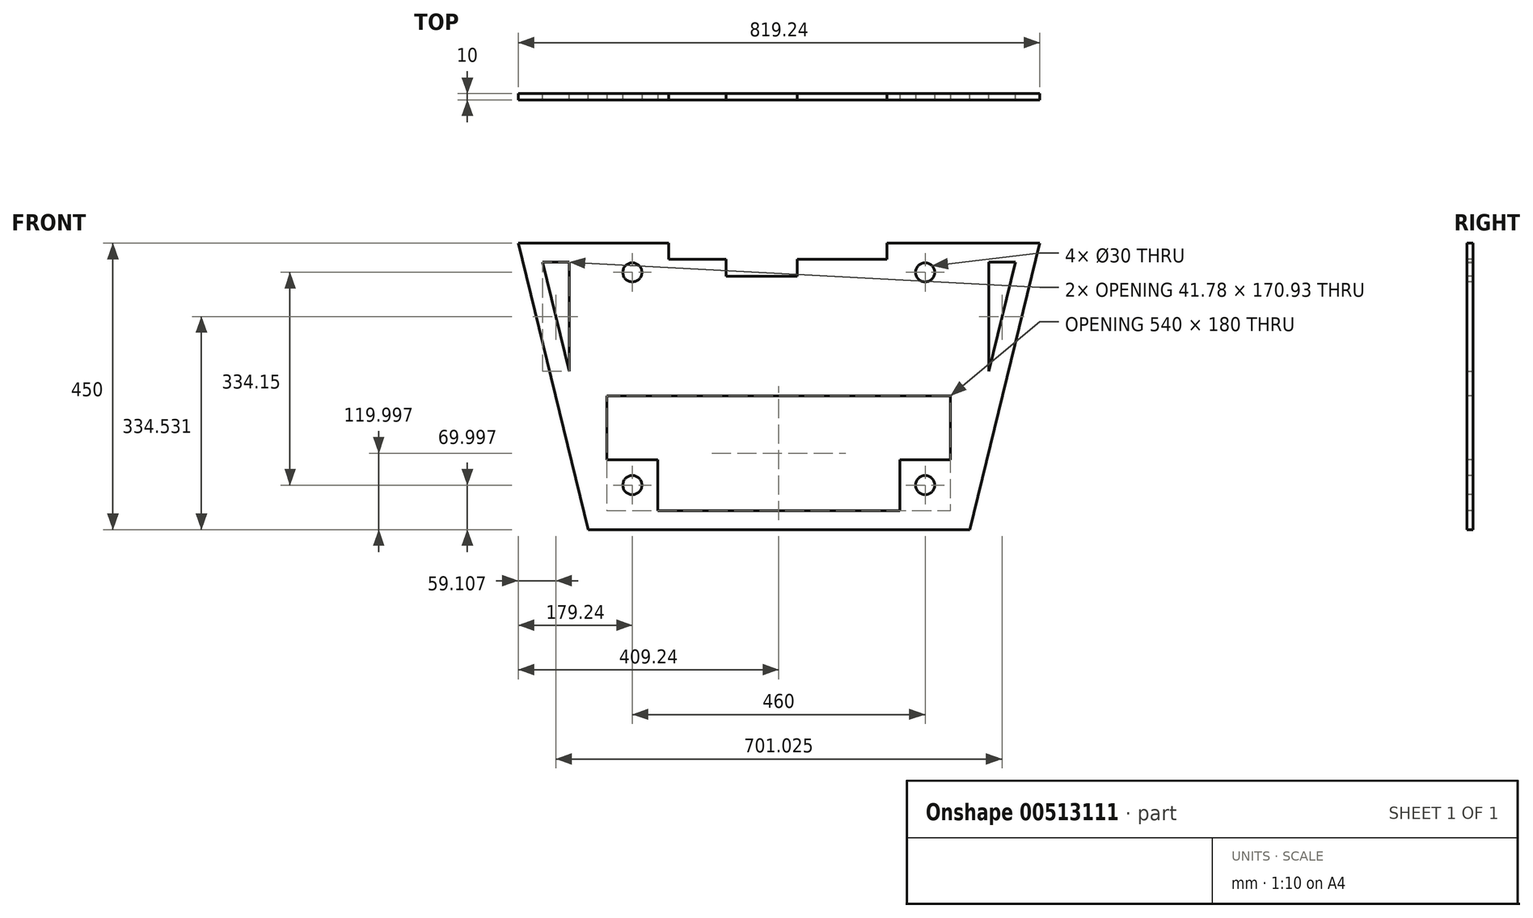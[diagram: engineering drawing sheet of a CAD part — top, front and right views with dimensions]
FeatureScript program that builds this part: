
annotation { "Feature Type Name" : "Feature", "Feature Type Description" : "" }
export const myFeature = defineFeature(function(context is Context, id is Id, definition is map)
    precondition{}
    {
        {
            var Q0;
            Q0=qCreatedBy(makeId("Front.planeOp"),FACE);
            var sketch = newSketch(context, id + "F0", { "sketchPlane" : qUnion([Q0])});
            skLineSegment(sketch, "E0.1", {"start": v(-436.34, 213.95) * mm, "end": v(-436.34, -176.05) * mm});
            skLineSegment(sketch, "E0.3", {"start": v(103.66, 213.95) * mm, "end": v(103.66, -176.05) * mm});
            skLineSegment(sketch, "E1", {"start": v(-465.58, -206.05) * mm, "end": v(133.66, -206.05) * mm});
            skLineSegment(sketch, "E2", {"start": v(-436.34, -176.05) * mm, "end": v(103.66, -176.05) * mm});
            skLineSegment(sketch, "E3", {"start": v(-436.34, 213.95) * mm, "end": v(103.66, 213.95) * mm});
            skLineSegment(sketch, "E4", {"start": v(-465.58, 243.95) * mm, "end": v(133.66, 243.95) * mm});
            skLineSegment(sketch, "E5", {"start": v(-465.58, 243.95) * mm, "end": v(-575.58, 243.95) * mm});
            skLineSegment(sketch, "E6", {"start": v(133.66, 243.95) * mm, "end": v(243.66, 243.95) * mm});
            skLineSegment(sketch, "E7", {"start": v(-575.58, 243.95) * mm, "end": v(-465.58, -206.05) * mm});
            skLineSegment(sketch, "E8", {"start": v(243.66, 243.95) * mm, "end": v(133.66, -206.05) * mm});
            skLineSegment(sketch, "E9.0", {"start": v(-537.36, 213.95) * mm, "end": v(-495.58, 43.02) * mm});
            skLineSegment(sketch, "E9.1", {"start": v(-495.58, 213.95) * mm, "end": v(-537.36, 213.95) * mm});
            skLineSegment(sketch, "E9.2", {"start": v(-495.58, 213.95) * mm, "end": v(-495.58, 43.02) * mm});
            skLineSegment(sketch, "E10.0", {"start": v(205.44, 213.95) * mm, "end": v(163.66, 43.02) * mm});
            skLineSegment(sketch, "E10.1", {"start": v(163.66, 213.95) * mm, "end": v(205.44, 213.95) * mm});
            skLineSegment(sketch, "E10.2", {"start": v(163.66, 213.95) * mm, "end": v(163.66, 43.02) * mm});
            skSolve(sketch);
        }
        {
            var Q0;
            Q0=makeQuery(id+"F0.imprint","IMPRINT",FACE,{"disambiguationData":[TD([[makeQuery(id+"F0.imprint","IMPRINT",EDGE,{"derivedFrom":sQuery(id+"F0.wireOp",EDGE,"E0.1")}),-1.0]])]});
            extrude(context, id + "F1", {"entities" : qUnion([Q0]), "depth" : 10 * mm, "offsetDistance" : 25 * mm});
        }
        {
            var Q0;
            Q0=makeQuery(id+"F1.opExtrude","CAP_FACE",FACE,{"disambiguationData":[OSD([sQuery(id+"F0.wireOp",EDGE,"E0.1"),sQuery(id+"F0.wireOp",EDGE,"E0.3"),sQuery(id+"F0.wireOp",EDGE,"E1"),sQuery(id+"F0.wireOp",EDGE,"E2"),sQuery(id+"F0.wireOp",EDGE,"E3"),sQuery(id+"F0.wireOp",EDGE,"E4"),sQuery(id+"F0.wireOp",EDGE,"E5"),sQuery(id+"F0.wireOp",EDGE,"E6"),sQuery(id+"F0.wireOp",EDGE,"E7"),sQuery(id+"F0.wireOp",EDGE,"E8"),sQuery(id+"F0.wireOp",EDGE,"E9.0"),sQuery(id+"F0.wireOp",EDGE,"E9.1"),sQuery(id+"F0.wireOp",EDGE,"E9.2"),sQuery(id+"F0.wireOp",EDGE,"E10.0"),sQuery(id+"F0.wireOp",EDGE,"E10.1"),sQuery(id+"F0.wireOp",EDGE,"E10.2")])],"isStart":false});
            var sketch = newSketch(context, id + "F2", { "sketchPlane" : qUnion([Q0])});
            skLineSegment(sketch, "E11.bottom", {"start": v(-436.34, 213.95) * mm, "end": v(-356.34, 213.95) * mm});
            skLineSegment(sketch, "E11.top", {"start": v(-436.34, 133.95) * mm, "end": v(-356.34, 133.95) * mm});
            skLineSegment(sketch, "E11.left", {"start": v(-436.34, 213.95) * mm, "end": v(-436.34, 133.95) * mm});
            skLineSegment(sketch, "E11.right", {"start": v(-356.34, 213.95) * mm, "end": v(-356.34, 133.95) * mm});
            skLineSegment(sketch, "E12.bottom", {"start": v(103.66, 213.95) * mm, "end": v(23.66, 213.95) * mm});
            skLineSegment(sketch, "E12.top", {"start": v(103.66, 133.95) * mm, "end": v(23.66, 133.95) * mm});
            skLineSegment(sketch, "E12.left", {"start": v(103.66, 213.95) * mm, "end": v(103.66, 133.95) * mm});
            skLineSegment(sketch, "E12.right", {"start": v(23.66, 213.95) * mm, "end": v(23.66, 133.95) * mm});
            skLineSegment(sketch, "E13.bottom", {"start": v(-436.34, -176.05) * mm, "end": v(-356.34, -176.05) * mm});
            skLineSegment(sketch, "E13.top", {"start": v(-436.34, -96.05) * mm, "end": v(-356.34, -96.05) * mm});
            skLineSegment(sketch, "E13.left", {"start": v(-436.34, -176.05) * mm, "end": v(-436.34, -96.05) * mm});
            skLineSegment(sketch, "E13.right", {"start": v(-356.34, -176.05) * mm, "end": v(-356.34, -96.05) * mm});
            skLineSegment(sketch, "E14.bottom", {"start": v(103.66, -176.05) * mm, "end": v(23.66, -176.05) * mm});
            skLineSegment(sketch, "E14.top", {"start": v(103.66, -96.05) * mm, "end": v(23.66, -96.05) * mm});
            skLineSegment(sketch, "E14.left", {"start": v(103.66, -176.05) * mm, "end": v(103.66, -96.05) * mm});
            skLineSegment(sketch, "E14.right", {"start": v(23.66, -176.05) * mm, "end": v(23.66, -96.05) * mm});
            skCircle(sketch, "E15", {"center": v(-396.34, -136.05) * mm, "radius": 15 * mm});
            skCircle(sketch, "E16", {"center": v(-396.34, 198.1) * mm, "radius": 15 * mm});
            skCircle(sketch, "E17", {"center": v(63.66, 198.1) * mm, "radius": 15 * mm});
            skCircle(sketch, "E18", {"center": v(63.66, -136.05) * mm, "radius": 15 * mm});
            skLineSegment(sketch, "E19", {"start": v(-356.34, 213.95) * mm, "end": v(-396.34, 243.95) * mm});
            skLineSegment(sketch, "E20", {"start": v(-356.34, 133.95) * mm, "end": v(23.66, 133.95) * mm});
            skLineSegment(sketch, "E21", {"start": v(23.66, 213.95) * mm, "end": v(63.66, 243.95) * mm});
            skLineSegment(sketch, "E22", {"start": v(-356.34, 213.95) * mm, "end": v(-249.67, 133.95) * mm});
            skLineSegment(sketch, "E23", {"start": v(23.66, 213.95) * mm, "end": v(-83, 133.95) * mm});
            skLineSegment(sketch, "E24", {"start": v(-396.34, 243.95) * mm, "end": v(63.66, 243.95) * mm});
            skSolve(sketch);
        }
        {
            var Q0;
            Q0=makeQuery(id+"F2.imprint","IMPRINT",FACE,{"disambiguationData":[TD([[makeQuery(id+"F2.imprint","IMPRINT",EDGE,{"derivedFrom":sQuery(id+"F2.wireOp",EDGE,"E11.bottom")}),-1.0]])]});
            var Q1;
            Q1=makeQuery(id+"F2.imprint","IMPRINT",FACE,{"disambiguationData":[TD([[makeQuery(id+"F2.imprint","IMPRINT",EDGE,{"derivedFrom":sQuery(id+"F2.wireOp",EDGE,"E12.bottom")}),-1.0]])]});
            var Q2;
            Q2=makeQuery(id+"F2.imprint","IMPRINT",FACE,{"disambiguationData":[TD([[makeQuery(id+"F2.imprint","IMPRINT",EDGE,{"derivedFrom":sQuery(id+"F2.wireOp",EDGE,"E14.bottom")}),1.0]])]});
            var Q3;
            Q3=makeQuery(id+"F2.imprint","IMPRINT",FACE,{"disambiguationData":[TD([[makeQuery(id+"F2.imprint","IMPRINT",EDGE,{"derivedFrom":sQuery(id+"F2.wireOp",EDGE,"E13.bottom")}),1.0]])]});
            extrude(context, id + "F3", {"entities" : qUnion([Q0, Q1, Q2, Q3]), "operationType" : NewBodyOperationType.ADD, "oppositeDirection" : true, "depth" : 10 * mm, "offsetDistance" : 25 * mm});
        }
        {
            var Q0;
            Q0=makeQuery(id+"F3.boolean.opBoolean","MERGE",FACE,{"derivedFrom":[makeQuery(id+"F1.opExtrude","CAP_FACE",FACE,{"disambiguationData":[OSD([sQuery(id+"F0.wireOp",EDGE,"E0.1"),sQuery(id+"F0.wireOp",EDGE,"E0.3"),sQuery(id+"F0.wireOp",EDGE,"E1"),sQuery(id+"F0.wireOp",EDGE,"E2"),sQuery(id+"F0.wireOp",EDGE,"E3"),sQuery(id+"F0.wireOp",EDGE,"E4"),sQuery(id+"F0.wireOp",EDGE,"E5"),sQuery(id+"F0.wireOp",EDGE,"E6"),sQuery(id+"F0.wireOp",EDGE,"E7"),sQuery(id+"F0.wireOp",EDGE,"E8"),sQuery(id+"F0.wireOp",EDGE,"E9.0"),sQuery(id+"F0.wireOp",EDGE,"E9.1"),sQuery(id+"F0.wireOp",EDGE,"E9.2"),sQuery(id+"F0.wireOp",EDGE,"E10.0"),sQuery(id+"F0.wireOp",EDGE,"E10.1"),sQuery(id+"F0.wireOp",EDGE,"E10.2")])],"isStart":false}),makeQuery(id+"F3.opExtrude","CAP_FACE",FACE,{"disambiguationData":[OSD([sQuery(id+"F2.wireOp",EDGE,"E11.bottom"),sQuery(id+"F2.wireOp",EDGE,"E11.top"),sQuery(id+"F2.wireOp",EDGE,"E11.left"),sQuery(id+"F2.wireOp",EDGE,"E11.right"),sQuery(id+"F2.wireOp",EDGE,"E16")])],"isStart":true}),makeQuery(id+"F3.opExtrude","CAP_FACE",FACE,{"disambiguationData":[OSD([sQuery(id+"F2.wireOp",EDGE,"E12.bottom"),sQuery(id+"F2.wireOp",EDGE,"E12.top"),sQuery(id+"F2.wireOp",EDGE,"E12.left"),sQuery(id+"F2.wireOp",EDGE,"E12.right"),sQuery(id+"F2.wireOp",EDGE,"E17")])],"isStart":true}),makeQuery(id+"F3.opExtrude","CAP_FACE",FACE,{"disambiguationData":[OSD([sQuery(id+"F2.wireOp",EDGE,"E13.bottom"),sQuery(id+"F2.wireOp",EDGE,"E13.top"),sQuery(id+"F2.wireOp",EDGE,"E13.left"),sQuery(id+"F2.wireOp",EDGE,"E13.right"),sQuery(id+"F2.wireOp",EDGE,"E15")])],"isStart":true}),makeQuery(id+"F3.opExtrude","CAP_FACE",FACE,{"disambiguationData":[OSD([sQuery(id+"F2.wireOp",EDGE,"E14.bottom"),sQuery(id+"F2.wireOp",EDGE,"E14.top"),sQuery(id+"F2.wireOp",EDGE,"E14.left"),sQuery(id+"F2.wireOp",EDGE,"E14.right"),sQuery(id+"F2.wireOp",EDGE,"E18")])],"isStart":true})]});
            var sketch = newSketch(context, id + "F4", { "sketchPlane" : qUnion([Q0])});
            skLineSegment(sketch, "E25", {"start": v(-356.34, 133.95) * mm, "end": v(23.66, 133.95) * mm});
            skLineSegment(sketch, "E26", {"start": v(-167.95, 292.5) * mm, "end": v(-335.9, 292.5) * mm});
            skLineSegment(sketch, "E27", {"start": v(-167.95, 292.5) * mm, "end": v(0, 292.5) * mm});
            skPoint(sketch, "E28.start.orphan", {"position": v(-166.34, 213.95) * mm});
            skLineSegment(sketch, "E29", {"start": v(-356.34, 243.95) * mm, "end": v(23.66, 243.95) * mm});
            skLineSegment(sketch, "E30", {"start": v(-286.97, 218.5) * mm, "end": v(3.6, 218.5) * mm});
            skLineSegment(sketch, "E31", {"start": v(-286.97, 218.5) * mm, "end": v(-339, 218.5) * mm});
            skPoint(sketch, "E32.orphan", {"position": v(-335.9, 213.95) * mm});
            skPoint(sketch, "E33.orphan", {"position": v(0, 213.95) * mm});
            skLineSegment(sketch, "E34", {"start": v(-339, 218.5) * mm, "end": v(-339, 243.95) * mm});
            skLineSegment(sketch, "E35", {"start": v(3.6, 218.5) * mm, "end": v(3.6, 243.95) * mm});
            skSolve(sketch);
        }
        {
            var Q0;
            Q0=makeQuery(id+"F3.boolean.opBoolean","MERGE",FACE,{"derivedFrom":[makeQuery(id+"F1.opExtrude","CAP_FACE",FACE,{"disambiguationData":[OSD([sQuery(id+"F0.wireOp",EDGE,"E0.1"),sQuery(id+"F0.wireOp",EDGE,"E0.3"),sQuery(id+"F0.wireOp",EDGE,"E1"),sQuery(id+"F0.wireOp",EDGE,"E2"),sQuery(id+"F0.wireOp",EDGE,"E3"),sQuery(id+"F0.wireOp",EDGE,"E4"),sQuery(id+"F0.wireOp",EDGE,"E5"),sQuery(id+"F0.wireOp",EDGE,"E6"),sQuery(id+"F0.wireOp",EDGE,"E7"),sQuery(id+"F0.wireOp",EDGE,"E8"),sQuery(id+"F0.wireOp",EDGE,"E9.0"),sQuery(id+"F0.wireOp",EDGE,"E9.1"),sQuery(id+"F0.wireOp",EDGE,"E9.2"),sQuery(id+"F0.wireOp",EDGE,"E10.0"),sQuery(id+"F0.wireOp",EDGE,"E10.1"),sQuery(id+"F0.wireOp",EDGE,"E10.2")])],"isStart":false}),makeQuery(id+"F3.opExtrude","CAP_FACE",FACE,{"disambiguationData":[OSD([sQuery(id+"F2.wireOp",EDGE,"E11.bottom"),sQuery(id+"F2.wireOp",EDGE,"E11.top"),sQuery(id+"F2.wireOp",EDGE,"E11.left"),sQuery(id+"F2.wireOp",EDGE,"E11.right"),sQuery(id+"F2.wireOp",EDGE,"E16")])],"isStart":true}),makeQuery(id+"F3.opExtrude","CAP_FACE",FACE,{"disambiguationData":[OSD([sQuery(id+"F2.wireOp",EDGE,"E12.bottom"),sQuery(id+"F2.wireOp",EDGE,"E12.top"),sQuery(id+"F2.wireOp",EDGE,"E12.left"),sQuery(id+"F2.wireOp",EDGE,"E12.right"),sQuery(id+"F2.wireOp",EDGE,"E17")])],"isStart":true}),makeQuery(id+"F3.opExtrude","CAP_FACE",FACE,{"disambiguationData":[OSD([sQuery(id+"F2.wireOp",EDGE,"E13.bottom"),sQuery(id+"F2.wireOp",EDGE,"E13.top"),sQuery(id+"F2.wireOp",EDGE,"E13.left"),sQuery(id+"F2.wireOp",EDGE,"E13.right"),sQuery(id+"F2.wireOp",EDGE,"E15")])],"isStart":true}),makeQuery(id+"F3.opExtrude","CAP_FACE",FACE,{"disambiguationData":[OSD([sQuery(id+"F2.wireOp",EDGE,"E14.bottom"),sQuery(id+"F2.wireOp",EDGE,"E14.top"),sQuery(id+"F2.wireOp",EDGE,"E14.left"),sQuery(id+"F2.wireOp",EDGE,"E14.right"),sQuery(id+"F2.wireOp",EDGE,"E18")])],"isStart":true})]});
            var sketch = newSketch(context, id + "F5", { "sketchPlane" : qUnion([Q0])});
            skLineSegment(sketch, "E36.bottom", {"start": v(-356.34, 213.95) * mm, "end": v(23.66, 213.95) * mm});
            skLineSegment(sketch, "E36.top", {"start": v(-356.34, 133.95) * mm, "end": v(23.66, 133.95) * mm});
            skLineSegment(sketch, "E36.left", {"start": v(-356.34, 213.95) * mm, "end": v(-356.34, 133.95) * mm});
            skLineSegment(sketch, "E36.right", {"start": v(23.66, 213.95) * mm, "end": v(23.66, 133.95) * mm});
            skSolve(sketch);
        }
        {
            var Q0;
            Q0=makeQuery(id+"F5.imprint","IMPRINT",FACE,{"disambiguationData":[TD([[makeQuery(id+"F5.imprint","IMPRINT",EDGE,{"derivedFrom":sQuery(id+"F5.wireOp",EDGE,"E36.bottom")}),-1.0]])]});
            extrude(context, id + "F6", {"entities" : qUnion([Q0]), "operationType" : NewBodyOperationType.ADD, "oppositeDirection" : true, "depth" : 10 * mm, "offsetDistance" : 25 * mm});
        }
        {
            var Q0;
            Q0=makeQuery(id+"F4.imprint","IMPRINT",FACE,{"disambiguationData":[TD([[makeQuery(id+"F4.imprint","IMPRINT",EDGE,{"derivedFrom":sQuery(id+"F4.wireOp",EDGE,"E30")}),1.0]])]});
            extrude(context, id + "F7", {"entities" : qUnion([Q0]), "operationType" : NewBodyOperationType.REMOVE, "oppositeDirection" : true, "depth" : 25 * mm, "offsetDistance" : 25 * mm});
        }
        {
            var Q0;
            Q0=makeQuery(id+"F6.boolean.opBoolean","MERGE",FACE,{"derivedFrom":[makeQuery(id+"F3.boolean.opBoolean","MERGE",FACE,{"derivedFrom":[makeQuery(id+"F1.opExtrude","CAP_FACE",FACE,{"disambiguationData":[OSD([sQuery(id+"F0.wireOp",EDGE,"E0.1"),sQuery(id+"F0.wireOp",EDGE,"E0.3"),sQuery(id+"F0.wireOp",EDGE,"E1"),sQuery(id+"F0.wireOp",EDGE,"E2"),sQuery(id+"F0.wireOp",EDGE,"E3"),sQuery(id+"F0.wireOp",EDGE,"E4"),sQuery(id+"F0.wireOp",EDGE,"E5"),sQuery(id+"F0.wireOp",EDGE,"E6"),sQuery(id+"F0.wireOp",EDGE,"E7"),sQuery(id+"F0.wireOp",EDGE,"E8"),sQuery(id+"F0.wireOp",EDGE,"E9.0"),sQuery(id+"F0.wireOp",EDGE,"E9.1"),sQuery(id+"F0.wireOp",EDGE,"E9.2"),sQuery(id+"F0.wireOp",EDGE,"E10.0"),sQuery(id+"F0.wireOp",EDGE,"E10.1"),sQuery(id+"F0.wireOp",EDGE,"E10.2")])],"isStart":false}),makeQuery(id+"F3.opExtrude","CAP_FACE",FACE,{"disambiguationData":[OSD([sQuery(id+"F2.wireOp",EDGE,"E11.bottom"),sQuery(id+"F2.wireOp",EDGE,"E11.top"),sQuery(id+"F2.wireOp",EDGE,"E11.left"),sQuery(id+"F2.wireOp",EDGE,"E11.right"),sQuery(id+"F2.wireOp",EDGE,"E16")])],"isStart":true}),makeQuery(id+"F3.opExtrude","CAP_FACE",FACE,{"disambiguationData":[OSD([sQuery(id+"F2.wireOp",EDGE,"E12.bottom"),sQuery(id+"F2.wireOp",EDGE,"E12.top"),sQuery(id+"F2.wireOp",EDGE,"E12.left"),sQuery(id+"F2.wireOp",EDGE,"E12.right"),sQuery(id+"F2.wireOp",EDGE,"E17")])],"isStart":true}),makeQuery(id+"F3.opExtrude","CAP_FACE",FACE,{"disambiguationData":[OSD([sQuery(id+"F2.wireOp",EDGE,"E13.bottom"),sQuery(id+"F2.wireOp",EDGE,"E13.top"),sQuery(id+"F2.wireOp",EDGE,"E13.left"),sQuery(id+"F2.wireOp",EDGE,"E13.right"),sQuery(id+"F2.wireOp",EDGE,"E15")])],"isStart":true}),makeQuery(id+"F3.opExtrude","CAP_FACE",FACE,{"disambiguationData":[OSD([sQuery(id+"F2.wireOp",EDGE,"E14.bottom"),sQuery(id+"F2.wireOp",EDGE,"E14.top"),sQuery(id+"F2.wireOp",EDGE,"E14.left"),sQuery(id+"F2.wireOp",EDGE,"E14.right"),sQuery(id+"F2.wireOp",EDGE,"E18")])],"isStart":true})]}),makeQuery(id+"F6.opExtrude","CAP_FACE",FACE,{"disambiguationData":[OSD([sQuery(id+"F5.wireOp",EDGE,"E36.bottom"),sQuery(id+"F5.wireOp",EDGE,"E36.top"),sQuery(id+"F5.wireOp",EDGE,"E36.left"),sQuery(id+"F5.wireOp",EDGE,"E36.right")])],"isStart":true})]});
            var sketch = newSketch(context, id + "F8", { "sketchPlane" : qUnion([Q0])});
            skLineSegment(sketch, "E37", {"start": v(-248.92, 218.6) * mm, "end": v(-248.92, 192.27) * mm});
            skLineSegment(sketch, "E38", {"start": v(-248.92, 192.27) * mm, "end": v(-137.15, 192.27) * mm});
            skLineSegment(sketch, "E39", {"start": v(-137.15, 192.27) * mm, "end": v(-137.15, 218.6) * mm});
            skLineSegment(sketch, "E40", {"start": v(-339, 218.5) * mm, "end": v(-249, 218.5) * mm});
            skLineSegment(sketch, "E41", {"start": v(-248.92, 218.6) * mm, "end": v(-137.15, 218.6) * mm});
            skSolve(sketch);
        }
        {
            var Q0;
            {var subQ0=sQuery(id+"F8.wireOp",EDGE,"E38");Q0=makeQuery(id+"F8.imprint","IMPRINT",FACE,{"disambiguationData":[TD([[makeQuery(id+"F8.imprint","IMPRINT",EDGE,{"derivedFrom":subQ0}),1.0]])]});}
            extrude(context, id + "F9", {"entities" : qUnion([Q0]), "operationType" : NewBodyOperationType.REMOVE, "oppositeDirection" : true, "depth" : 25 * mm, "offsetDistance" : 25 * mm});
        }
        {
            var Q0;
            Q0=makeQuery(id+"F6.boolean.opBoolean","MERGE",FACE,{"derivedFrom":[makeQuery(id+"F3.opExtrude","SWEPT_FACE",FACE,{"disambiguationData":[OSD([sQuery(id+"F2.wireOp",EDGE,"E11.top")])]}),makeQuery(id+"F3.opExtrude","SWEPT_FACE",FACE,{"disambiguationData":[OSD([sQuery(id+"F2.wireOp",EDGE,"E12.top")])]}),makeQuery(id+"F6.opExtrude","SWEPT_FACE",FACE,{"disambiguationData":[OSD([sQuery(id+"F5.wireOp",EDGE,"E36.top")])]})]});
            extrude(context, id + "F10", {"entities" : qUnion([Q0]), "operationType" : NewBodyOperationType.ADD, "depth" : 130 * mm, "offsetDistance" : 25 * mm});
        }
    });
